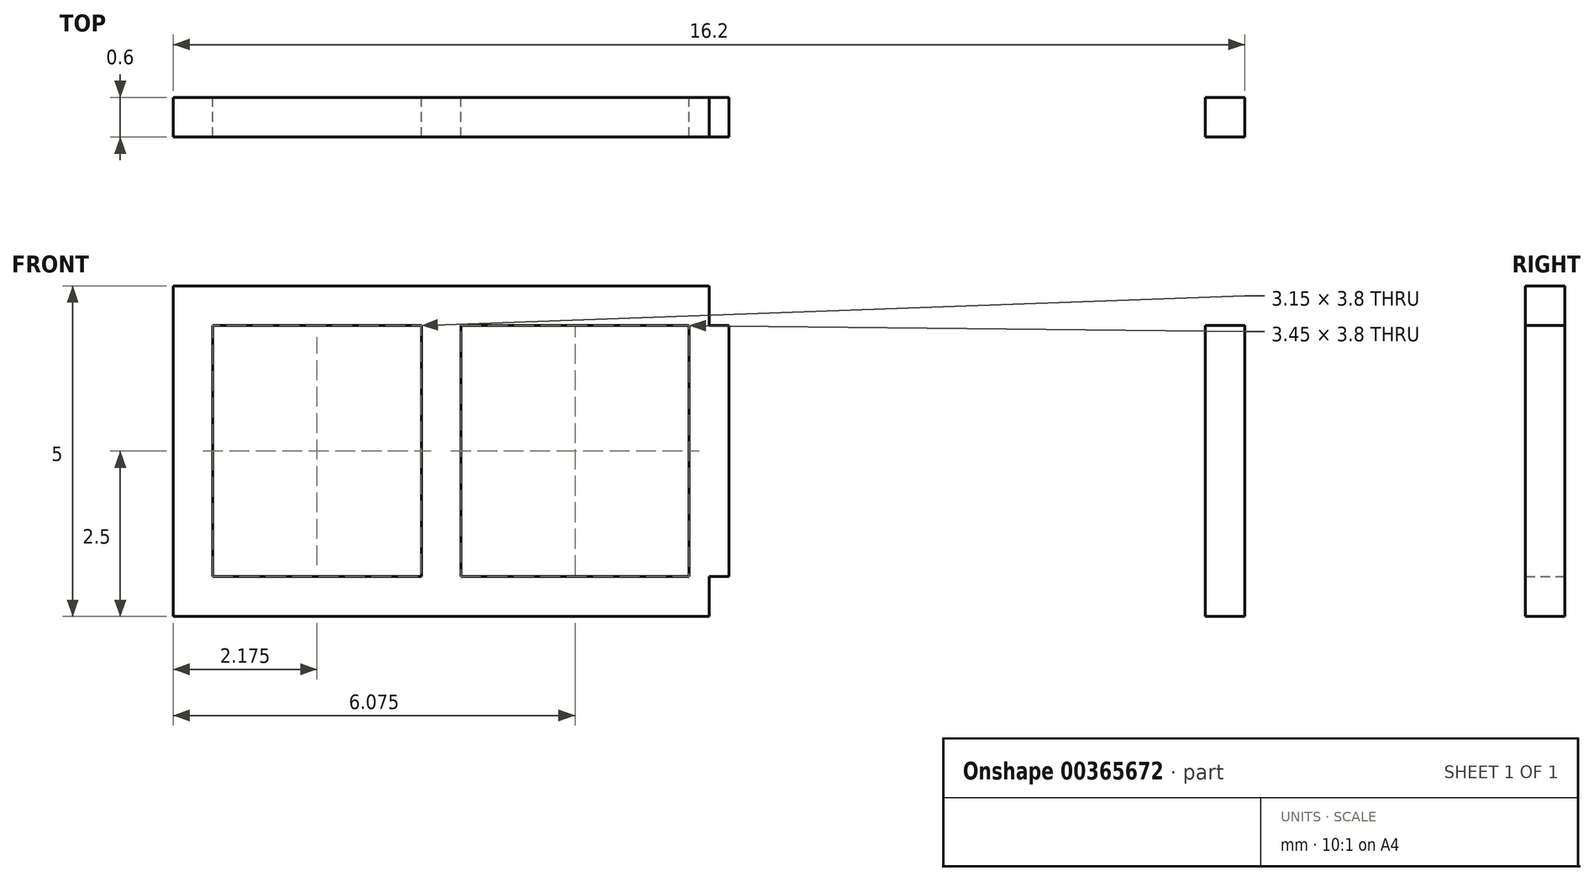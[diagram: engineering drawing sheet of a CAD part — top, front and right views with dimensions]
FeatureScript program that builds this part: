
annotation { "Feature Type Name" : "Feature", "Feature Type Description" : "" }
export const myFeature = defineFeature(function(context is Context, id is Id, definition is map)
    precondition{}
    {
        {
            var Q0;
            Q0=qCreatedBy(makeId("Front.planeOp"),FACE);
            var sketch = newSketch(context, id + "F0", { "sketchPlane" : qUnion([Q0])});
            skLineSegment(sketch, "E0.bottom", {"start": v(0, 0) * mm, "end": v(8.1, 0) * mm});
            skLineSegment(sketch, "E0.top", {"start": v(0, 0.6) * mm, "end": v(8.1, 0.6) * mm});
            skLineSegment(sketch, "E0.left", {"start": v(0, 0) * mm, "end": v(0, 0.6) * mm});
            skLineSegment(sketch, "E0.right", {"start": v(8.1, 0) * mm, "end": v(8.1, 0.6) * mm});
            skLineSegment(sketch, "E1.bottom", {"start": v(8.1, 0) * mm, "end": v(7.5, 0) * mm});
            skLineSegment(sketch, "E1.top", {"start": v(8.1, 5) * mm, "end": v(7.5, 5) * mm});
            skLineSegment(sketch, "E1.left", {"start": v(8.1, 0) * mm, "end": v(8.1, 5) * mm});
            skLineSegment(sketch, "E1.right", {"start": v(7.5, 0) * mm, "end": v(7.5, 5) * mm});
            skLineSegment(sketch, "E2.bottom", {"start": v(8.1, 5) * mm, "end": v(0, 5) * mm});
            skLineSegment(sketch, "E2.top", {"start": v(8.1, 4.4) * mm, "end": v(0, 4.4) * mm});
            skLineSegment(sketch, "E2.left", {"start": v(8.1, 5) * mm, "end": v(8.1, 4.4) * mm});
            skLineSegment(sketch, "E2.right", {"start": v(0, 5) * mm, "end": v(0, 4.4) * mm});
            skLineSegment(sketch, "E3", {"start": v(0, 7.83) * mm, "end": v(0, 0) * mm});
            skLineSegment(sketch, "E4.MirrorCS", {"start": v(-8.1, 5) * mm, "end": v(0, 5) * mm});
            skLineSegment(sketch, "E5.MirrorCS", {"start": v(-8.1, 4.4) * mm, "end": v(0, 4.4) * mm});
            skLineSegment(sketch, "E6.MirrorCS", {"start": v(0, 0.6) * mm, "end": v(-8.1, 0.6) * mm});
            skLineSegment(sketch, "E7.MirrorCS", {"start": v(0, 0) * mm, "end": v(-8.1, 0) * mm});
            skLineSegment(sketch, "E8.MirrorCS", {"start": v(-7.5, 0) * mm, "end": v(-7.5, 5) * mm});
            skLineSegment(sketch, "E9.MirrorCS", {"start": v(-8.1, 0) * mm, "end": v(-8.1, 5) * mm});
            skLineSegment(sketch, "E10", {"start": v(0.3, 4.4) * mm, "end": v(0.3, 0.6) * mm});
            skLineSegment(sketch, "E11.MirrorCS", {"start": v(-0.3, 4.4) * mm, "end": v(-0.3, 0.6) * mm});
            skPoint(sketch, "E12", {"position": v(4.05, 4.4) * mm});
            skPoint(sketch, "E13", {"position": v(3.75, 4.4) * mm});
            skPoint(sketch, "E14", {"position": v(4.35, 4.4) * mm});
            skPoint(sketch, "E15.oppositeSnap0", {"position": v(4.05, 0.6) * mm});
            skLineSegment(sketch, "E15.bottom", {"start": v(3.75, 4.4) * mm, "end": v(4.35, 4.4) * mm});
            skLineSegment(sketch, "E15.top", {"start": v(3.75, 0.6) * mm, "end": v(4.35, 0.6) * mm});
            skLineSegment(sketch, "E15.left", {"start": v(3.75, 4.4) * mm, "end": v(3.75, 0.6) * mm});
            skLineSegment(sketch, "E15.right", {"start": v(4.35, 4.4) * mm, "end": v(4.35, 0.6) * mm});
            skLineSegment(sketch, "E16.MirrorCS", {"start": v(-3.75, 4.4) * mm, "end": v(-3.75, 0.6) * mm});
            skLineSegment(sketch, "E17.MirrorCS", {"start": v(-4.35, 4.4) * mm, "end": v(-4.35, 0.6) * mm});
            skSolve(sketch);
        }
        {
            var Q0;
            {var subQ5=sQuery(id+"F0.wireOp",EDGE,"E11.MirrorCS");Q0=makeQuery(id+"F0.imprint","IMPRINT",FACE,{"disambiguationData":[TD([[makeQuery(id+"F0.imprint","IMPRINT",EDGE,{"derivedFrom":subQ5}),1.0]])]});}
            var Q1;
            {var subQ0=sQuery(id+"F0.wireOp",EDGE,"E9.MirrorCS");var subQ1=sQuery(id+"F0.wireOp",EDGE,"E6.MirrorCS");var subQ2=makeQuery(id+"F0.imprint","INTERSECT",VERTEX,{"derivedFrom":[subQ1,subQ0]});Q1=makeQuery(id+"F0.imprint","IMPRINT",FACE,{"disambiguationData":[TD([[makeQuery(id+"F0.imprint","IMPRINT",EDGE,{"disambiguationData":[TD([[subQ2,1.0]])],"derivedFrom":subQ1}),1.0]])]});}
            var Q2;
            {var subQ0=sQuery(id+"F0.wireOp",EDGE,"E9.MirrorCS");var subQ1=sQuery(id+"F0.wireOp",EDGE,"E5.MirrorCS");var subQ2=makeQuery(id+"F0.imprint","INTERSECT",VERTEX,{"derivedFrom":[subQ1,subQ0]});Q2=makeQuery(id+"F0.imprint","IMPRINT",FACE,{"disambiguationData":[TD([[makeQuery(id+"F0.imprint","IMPRINT",EDGE,{"disambiguationData":[TD([[subQ2,-1.0]])],"derivedFrom":subQ1}),-1.0]])]});}
            var Q3;
            {var subQ0=sQuery(id+"F0.wireOp",EDGE,"E15.bottom");Q3=makeQuery(id+"F0.imprint","IMPRINT",FACE,{"disambiguationData":[TD([[makeQuery(id+"F0.imprint","IMPRINT",EDGE,{"derivedFrom":subQ0}),1.0]])]});}
            var Q4;
            {var subQ0=sQuery(id+"F0.wireOp",EDGE,"E5.MirrorCS");var subQ2=makeQuery(id+"F0.imprint","INTERSECT",VERTEX,{"derivedFrom":[subQ0,sQuery(id+"F0.wireOp",EDGE,"E17.MirrorCS")]});Q4=makeQuery(id+"F0.imprint","IMPRINT",FACE,{"disambiguationData":[TD([[makeQuery(id+"F0.imprint","IMPRINT",EDGE,{"disambiguationData":[TD([[subQ2,1.0]])],"derivedFrom":subQ0}),1.0]])]});}
            var Q5;
            {var subQ3=sQuery(id+"F0.wireOp",EDGE,"E10");Q5=makeQuery(id+"F0.imprint","IMPRINT",FACE,{"disambiguationData":[TD([[makeQuery(id+"F0.imprint","IMPRINT",EDGE,{"derivedFrom":subQ3}),-1.0]])]});}
            var Q6;
            Q6=makeQuery(id+"F0.imprint","IMPRINT",FACE,{"disambiguationData":[TD([[makeQuery(id+"F0.imprint","IMPRINT",EDGE,{"derivedFrom":sQuery(id+"F0.wireOp",EDGE,"E15.bottom")}),-1.0]])]});
            var Q7;
            {var subQ0=sQuery(id+"F0.wireOp",EDGE,"E1.left");var subQ1=sQuery(id+"F0.wireOp",EDGE,"E0.top");var subQ2=makeQuery(id+"F0.imprint","INTERSECT",VERTEX,{"derivedFrom":[subQ1,subQ0]});Q7=makeQuery(id+"F0.imprint","IMPRINT",FACE,{"disambiguationData":[TD([[makeQuery(id+"F0.imprint","IMPRINT",EDGE,{"disambiguationData":[TD([[subQ2,1.0]])],"derivedFrom":subQ1}),1.0]])]});}
            var Q8;
            {var subQ0=sQuery(id+"F0.wireOp",EDGE,"E9.MirrorCS");var subQ1=sQuery(id+"F0.wireOp",EDGE,"E4.MirrorCS");var subQ2=makeQuery(id+"F0.imprint","INTERSECT",VERTEX,{"derivedFrom":[subQ1,subQ0]});Q8=makeQuery(id+"F0.imprint","IMPRINT",FACE,{"disambiguationData":[TD([[makeQuery(id+"F0.imprint","IMPRINT",EDGE,{"disambiguationData":[TD([[subQ2,-1.0]])],"derivedFrom":subQ1}),-1.0]])]});}
            var Q9;
            {var subQ0=sQuery(id+"F0.wireOp",EDGE,"E6.MirrorCS");var subQ1=makeQuery(id+"F0.imprint","INTERSECT",VERTEX,{"derivedFrom":[subQ0,sQuery(id+"F0.wireOp",EDGE,"E11.MirrorCS")]});Q9=makeQuery(id+"F0.imprint","IMPRINT",FACE,{"disambiguationData":[TD([[makeQuery(id+"F0.imprint","IMPRINT",EDGE,{"disambiguationData":[TD([[subQ1,-1.0]])],"derivedFrom":subQ0}),1.0]])]});}
            var Q10;
            {var subQ5=sQuery(id+"F0.wireOp",EDGE,"E1.bottom");Q10=makeQuery(id+"F0.imprint","IMPRINT",FACE,{"disambiguationData":[TD([[makeQuery(id+"F0.imprint","IMPRINT",EDGE,{"derivedFrom":subQ5}),-1.0]])]});}
            var Q11;
            {var subQ0=sQuery(id+"F0.wireOp",EDGE,"E16.MirrorCS");Q11=makeQuery(id+"F0.imprint","IMPRINT",FACE,{"disambiguationData":[TD([[makeQuery(id+"F0.imprint","IMPRINT",EDGE,{"derivedFrom":subQ0}),-1.0]])]});}
            var Q12;
            {var subQ7=sQuery(id+"F0.wireOp",EDGE,"E0.bottom");Q12=makeQuery(id+"F0.imprint","IMPRINT",FACE,{"disambiguationData":[TD([[makeQuery(id+"F0.imprint","IMPRINT",EDGE,{"derivedFrom":subQ7}),1.0]])]});}
            var Q13;
            {var subQ5=sQuery(id+"F0.wireOp",EDGE,"E2.left");Q13=makeQuery(id+"F0.imprint","IMPRINT",FACE,{"disambiguationData":[TD([[makeQuery(id+"F0.imprint","IMPRINT",EDGE,{"derivedFrom":subQ5}),-1.0]])]});}
            extrude(context, id + "F1", {"entities" : qUnion([Q0, Q1, Q2, Q3, Q4, Q5, Q6, Q7, Q8, Q9, Q10, Q11, Q12, Q13]), "depth" : 0.6 * mm});
        }
    });
